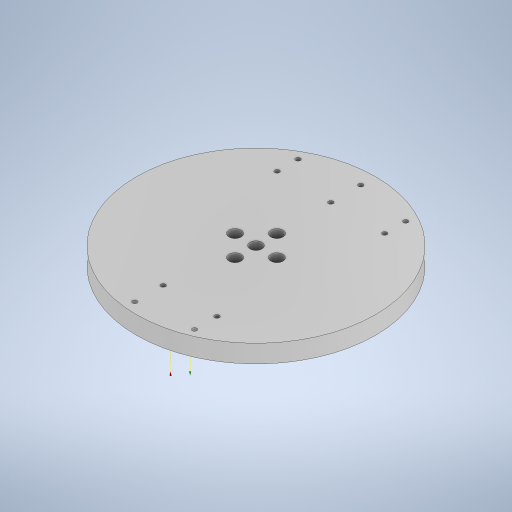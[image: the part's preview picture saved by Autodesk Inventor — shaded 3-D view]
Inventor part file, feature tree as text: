
AUTODESK INVENTOR PART (.ipt)
format: ipt  version: 2024.2 (Build 282272000, 272)  size: 454,656 bytes
history: native  units: in
note: dims shown in document units (in); Inventor stores cm internally (conversion verified against a paired STEP export)
features: reference x17, sketch x7, extrude x5, other x5, hole x2, projected_geometry x1
ambient origin geometry x8: Origin, YZ Plane, XZ Plane, XY Plane, X Axis, Y Axis, Z Axis, Center Point
bodies: Solid1 (feature_tree)
feature tree (37):
  extrude  "Extrusion1"  Depth=0.2362in TaperAngle=0.0deg
  extrude  "Extrusion2"  Depth=0.0787in
  hole  "Hole1"  [1 undecoded]
  extrude  "Extrusion3"  Depth=0.0591in TaperAngle=0.0deg
  extrude  "Extrusion4"  Depth=0.1181in
  extrude  "Extrusion5"  [1 undecoded]
  hole  "Hole2"  [1 undecoded]
  sketch  "Sketch1"  dims[d0=3.1496in d1=0.2362in d2=0.0in]
  sketch  "Sketch2"  dims[d3=0.0563in d4=0.0in]
  reference  "Reference1"
  reference  "Reference2"
  sketch  "Sketch3"  dims[d5=0.0827in d6=0.2362in d7=0.119in d8=0.0787in d9=0.5635in d10=0.315in d11=0.8108in d12=0.1614in]
  reference  "Reference3"
  reference  "Reference4"
  reference  "Reference5"
  reference  "Reference6"
  sketch  "Sketch4"  dims[d13=0.1181in d14=0.0in d15=0.0in d16=0.0in]
  projected_geometry  "Projected Loop1"
  sketch  "Sketch5"  dims[d17=0.2362in d18=0.0591in d19=0.0in]
  reference  "Reference7"
  sketch  "Sketch6"  dims[d20=0.0617in d21=0.1181in d22=0.1575in d23=0.0787in d24=90.0deg d25=0.1181in d26=0.0in d27=0.1575in]
  sketch  "Sketch7"
  reference  "Reference8"
  reference  "Reference9"
  reference  "Reference10"
  reference  "Reference11"
  reference  "Reference12"
  reference  "Reference13"
  reference  "Reference14"
  reference  "Reference15"
  reference  "Reference16"
  reference  "Reference17"
  other  "2_Arm.iam"
  other  "axis_1_top_frame:1"
  other  "Top Horn:1"
  other  "axis_2_bottom_L_frame(top):1"
  other  "axis_2_bottom_L_frame(bottom):1"
note: 3 required parameter values undecoded (feature->parameter linkage not recoverable at this tier; creation-order binding heuristic only, values carry confidence <= 0.55)
